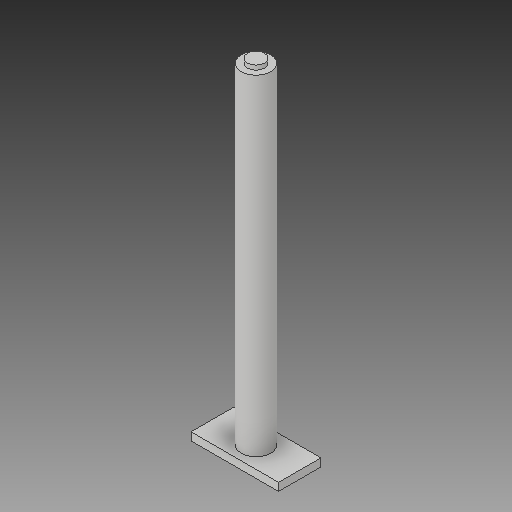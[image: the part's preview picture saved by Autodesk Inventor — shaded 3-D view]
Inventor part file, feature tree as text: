
AUTODESK INVENTOR PART (.ipt)
format: ipt  version: 2018 (Build 220112000, 112)  size: 110,080 bytes
history: native  units: in
note: dims shown in document units (in); Inventor stores cm internally (conversion verified against a paired STEP export)
features: extrude x4, sketch x4
ambient origin geometry x8: Origin, YZ Plane, XZ Plane, XY Plane, X Axis, Y Axis, Z Axis, Center Point
bodies: Solid1 (feature_tree)
feature tree (8):
  extrude  "Extrusion1"  Depth=2.8976in TaperAngle=0.0deg
  extrude  "Extrusion2"  Depth=2.7874in TaperAngle=0.0deg
  extrude  "Extrusion3"  Depth=0.0394in
  extrude  "Extrusion4"  Depth=0.0689in
  sketch  "Sketch1"  dims[d0=0.2579in d1=2.8976in d2=0.0in]
  sketch  "Sketch2"  dims[d3=0.1496in d4=2.7874in d5=0.0in]
  sketch  "Sketch3"  dims[d6=0.0394in d7=0.0in d8=0.186in]
  sketch  "Sketch4"  dims[d9=0.372in d10=0.3839in d11=0.7677in d12=0.0689in d13=0.0in]
